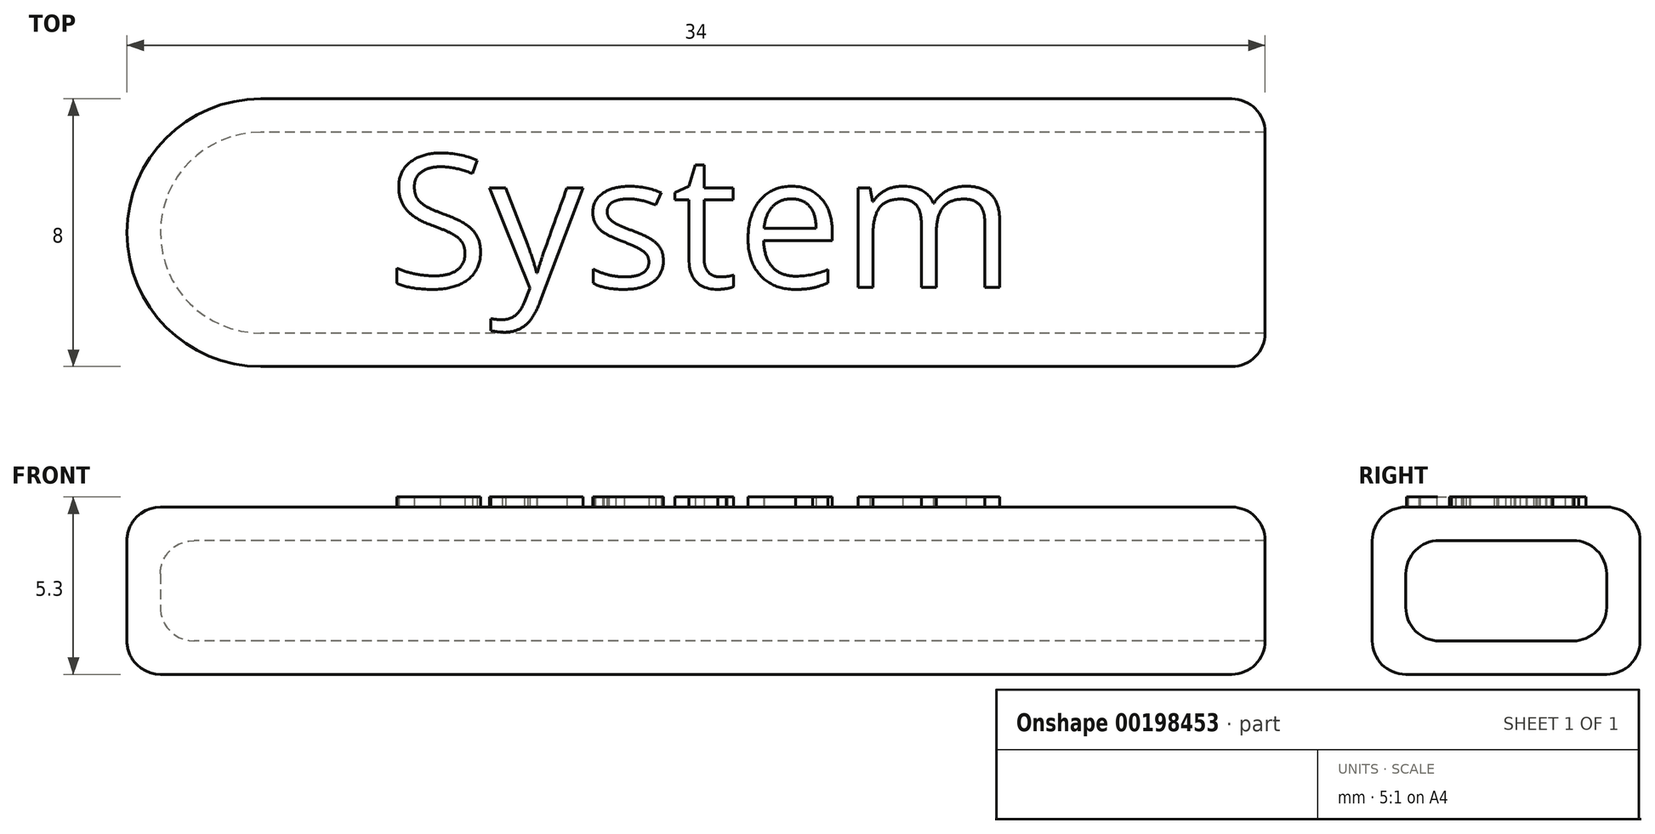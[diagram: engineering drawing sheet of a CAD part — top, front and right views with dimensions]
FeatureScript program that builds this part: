
annotation { "Feature Type Name" : "Feature", "Feature Type Description" : "" }
export const myFeature = defineFeature(function(context is Context, id is Id, definition is map)
    precondition{}
    {
        {
            var Q0;
            Q0=qCreatedBy(makeId("Top.planeOp"),FACE);
            var sketch = newSketch(context, id + "F0", { "sketchPlane" : qUnion([Q0])});
            skArc(sketch, "E0", {"start": v(-17.23, 4) * mm, "mid": v(-21.23, 0) * mm, "end": v(-17.23, -4) * mm});
            skLineSegment(sketch, "E1", {"start": v(-17.23, 4) * mm, "end": v(12.77, 4) * mm});
            skLineSegment(sketch, "E2", {"start": v(-17.23, -4) * mm, "end": v(12.77, -4) * mm});
            skLineSegment(sketch, "E3", {"start": v(12.77, 4) * mm, "end": v(12.77, -4) * mm});
            skSolve(sketch);
        }
        {
            var Q0;
            Q0 = qSketchRegion(id + "F0", true);
            extrude(context, id + "F1", {"entities" : qUnion([Q0]), "depth" : 5 * mm});
        }
        {
            var Q0;
            Q0=makeQuery(id+"F1.opExtrude","CAP_FACE",FACE,{"disambiguationData":[OSD([sQuery(id+"F0.wireOp",EDGE,"E0"),sQuery(id+"F0.wireOp",EDGE,"E1"),sQuery(id+"F0.wireOp",EDGE,"E2"),sQuery(id+"F0.wireOp",EDGE,"E3")])],"isStart":false});
            var Q1;
            Q1=makeQuery(id+"F1.opExtrude","CAP_FACE",FACE,{"disambiguationData":[OSD([sQuery(id+"F0.wireOp",EDGE,"E0"),sQuery(id+"F0.wireOp",EDGE,"E1"),sQuery(id+"F0.wireOp",EDGE,"E2"),sQuery(id+"F0.wireOp",EDGE,"E3")])],"isStart":true});
            fillet(context, id + "F2", {"entities" : qUnion([Q0, Q1]), "radius" : 1 * mm, "tangentPropagation" : true, "defaultsChanged" : false, "vertexSettings" : [], "allowEdgeOverflow" : false});
        }
        {
            var Q0;
            Q0=makeQuery(id+"F1.opExtrude","SWEPT_FACE",FACE,{"disambiguationData":[OSD([sQuery(id+"F0.wireOp",EDGE,"E3")])]});
            shell(context, id + "F3", {"entities" : qUnion([Q0]), "thickness" : 1 * mm});
        }
        {
            var Q0;
            {var subQ0=sQuery(id+"F0.wireOp",EDGE,"E2");var subQ1=makeQuery(id+"F1.opExtrude","CAP_EDGE",EDGE,{"disambiguationData":[OSD([subQ0])],"isStart":true});var subQ2=sQuery(id+"F0.wireOp",EDGE,"E3");var subQ3=sQuery(id+"F0.wireOp",EDGE,"E1");var subQ4=sQuery(id+"F0.wireOp",EDGE,"E0");Q0=makeQuery(id+"F3.opShell","OFFSET_EDGE",EDGE,{"disambiguationData":[OSD([subQ4,subQ3,subQ0,subQ2]),TDD([makeQuery(id+"F2.opFillet","BLEND_EDGE",EDGE,{"blendedFrom":[subQ1,makeQuery(id+"F1.opExtrude","CAP_FACE",FACE,{"disambiguationData":[OSD([subQ4,subQ3,subQ0,subQ2])],"isStart":true})],"blendedInto":[makeQuery(id+"F1.opExtrude","CAP_FACE",FACE,{"disambiguationData":[OSD([subQ4,subQ3,subQ0,subQ2])],"isStart":true})]}),makeQuery(id+"F2.opFillet","BLEND_EDGE",EDGE,{"blendedFrom":[subQ1,makeQuery(id+"F1.opExtrude","SWEPT_FACE",FACE,{"disambiguationData":[OSD([subQ0])]})],"blendedInto":[makeQuery(id+"F1.opExtrude","SWEPT_FACE",FACE,{"disambiguationData":[OSD([subQ0])]})]})])]});}
            var Q1;
            {var subQ0=sQuery(id+"F0.wireOp",EDGE,"E2");var subQ1=makeQuery(id+"F1.opExtrude","CAP_EDGE",EDGE,{"disambiguationData":[OSD([subQ0])],"isStart":false});var subQ2=sQuery(id+"F0.wireOp",EDGE,"E3");var subQ3=sQuery(id+"F0.wireOp",EDGE,"E1");var subQ4=sQuery(id+"F0.wireOp",EDGE,"E0");Q1=makeQuery(id+"F3.opShell","OFFSET_EDGE",EDGE,{"disambiguationData":[OSD([subQ4,subQ3,subQ0,subQ2]),TDD([makeQuery(id+"F2.opFillet","BLEND_EDGE",EDGE,{"blendedFrom":[subQ1,makeQuery(id+"F1.opExtrude","CAP_FACE",FACE,{"disambiguationData":[OSD([subQ4,subQ3,subQ0,subQ2])],"isStart":false})],"blendedInto":[makeQuery(id+"F1.opExtrude","CAP_FACE",FACE,{"disambiguationData":[OSD([subQ4,subQ3,subQ0,subQ2])],"isStart":false})]}),makeQuery(id+"F2.opFillet","BLEND_EDGE",EDGE,{"blendedFrom":[subQ1,makeQuery(id+"F1.opExtrude","SWEPT_FACE",FACE,{"disambiguationData":[OSD([subQ0])]})],"blendedInto":[makeQuery(id+"F1.opExtrude","SWEPT_FACE",FACE,{"disambiguationData":[OSD([subQ0])]})]})])]});}
            fillet(context, id + "F4", {"entities" : qUnion([Q0, Q1]), "radius" : 1 * mm, "tangentPropagation" : true, "defaultsChanged" : false, "vertexSettings" : [], "allowEdgeOverflow" : false});
        }
        {
            var Q0;
            Q0=makeQuery(id+"F1.opExtrude","CAP_FACE",FACE,{"disambiguationData":[OSD([sQuery(id+"F0.wireOp",EDGE,"E0"),sQuery(id+"F0.wireOp",EDGE,"E1"),sQuery(id+"F0.wireOp",EDGE,"E2"),sQuery(id+"F0.wireOp",EDGE,"E3")])],"isStart":false});
            var sketch = newSketch(context, id + "F5", { "sketchPlane" : qUnion([Q0])});
            skText(sketch, "E4", { "text": "System", "fontName": "OpenSans-Regular.ttf"});
            const initialGuessF5  = {"E4": [-0.01345, -0.00164, 1, 0, 0.004]};
            skSetInitialGuess(sketch, initialGuessF5);
            skSolve(sketch);
        }
        {
            var Q0;
            Q0 = qSketchRegion(id + "F5", true);
            extrude(context, id + "F6", {"entities" : qUnion([Q0]), "operationType" : NewBodyOperationType.ADD, "depth" : 0.3 * mm});
        }
        {
            var Q0;
            Q0=makeQuery(id+"F1.opExtrude","SWEPT_EDGE",EDGE,{"disambiguationData":[OSD([sQuery(id+"F0.wireOp",EDGE,"E1"),sQuery(id+"F0.wireOp",EDGE,"E3")])]});
            var Q1;
            Q1=makeQuery(id+"F1.opExtrude","SWEPT_EDGE",EDGE,{"disambiguationData":[OSD([sQuery(id+"F0.wireOp",EDGE,"E2"),sQuery(id+"F0.wireOp",EDGE,"E3")])]});
            fillet(context, id + "F7", {"entities" : qUnion([Q0, Q1]), "radius" : 1 * mm, "tangentPropagation" : true, "allowEdgeOverflow" : false});
        }
    });
